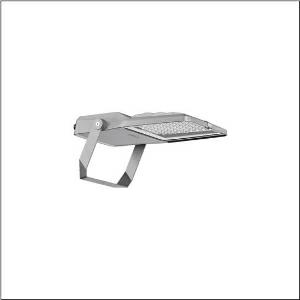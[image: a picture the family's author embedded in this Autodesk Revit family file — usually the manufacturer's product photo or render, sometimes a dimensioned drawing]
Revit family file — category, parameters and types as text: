
# Revit family: floodlight_fl_21_mini___pl52_5xa7773c4d1a_b58d
name_source: partatom
category: Lighting Fixtures
units: mm (PartAtom-declared; Revit-internal decimal feet)

## family parameters
Cut with Voids When Loaded = No
Host = Face
Light Source = No
Part Type = Normal
Room Calculation Point = No
Round Connector Dimension = Use Diameter
Shared = No

## types (1)
- --- (1 x LED, 20360 lm, 163.5 W, 4000K)
    Apparent Load = 163 VA
    CIE Flux Codes = 26 60 98 100 100
    Color Rendering = 70
    Color Temperature = 4000K
    Default Elevation = 1800 mm
    Description = Floodlight FL 21 mini, floodlight, primary light control with lens, of PMMA, primary optical cover: protective disc, of toughened safety glass, transparent, light distribution: PL52, light emission: direct distribution, installation type: surface-mounted, LED, High Power LED, rated luminous flux: 20.360lm, luminous efficacy: 125lm/W, light colour: 740, colour temperature: 4000K, control gear: ON/OFF Multilumen, control: Temp-Guard, with terminal, 6-pole, mains connection: 220..240V, AC, 50/60Hz, start of lifetime: 164W, luminaire housing, of diecast aluminium, powder-coated, Siteco® metallic grey (DB 702S), corrosivity category C5 mid according to DIN EN ISO 12944, suitable for swimming pools, chlorine-resistant, sealing non-destructively replaceable, mounting bracket, of steel, galvanised, powder-coated, Siteco® metallic grey (DB 702S), ON/OFF, protection rating (complete): IP66, insulation class (complete): insulation class I (protective earthing), certification: CE, ENEC, VDE, protection symbol: D, impact resistance: IK08, permissible operating ambient temperature: -40..+40°C, permissible operating ambient temperature for outdoor applications: -40..+50°C, standard: DIN EN 12944, LABS conformity tested according to VDMA 24364:2018-05, packaging unit: 1 piece

Light Distribution: PL52
    Height = 70 mm
    Lamp = 1 x LED
    Lamp Light Flux = 20360 lm
    Lamp Power = 163.5 W
    Lamp count = 1
    Length = 485 mm
    Luminous efficacy = 125 lm/W
    Manufacturer = Siteco
    ModVariant = No
    Model = 5XA7773C4D1A
    Number of Poles = 1
    OnlyDefault = Yes
    Power Factor = 1
    Product Name = Floodlight FL 21 mini | PL52
    Product group = floodlight | pylon annexe
    ProductGroupID = 6200
    Protection Class = Protection class I
    Protection Degree = IP 66
    RLX_Detail_Level = 1
    RLX_Emergency_Light_Flux = 0 lm
    RLX_Emergency_Type = 0
    RLX_Emergency_Type_DB = No
    RlxData = <blob elided: 94457 chars, md5=790c923c>
    Socket = socket
    Standby Power = 0 W
    System Light Flux = 20360 lm
    System Power = 163 W
    Type Comments = factory setting: luminous flux: 100 % | (ON | - | - | - | - | - | - | -) | 825 mA
    Type Image = l_1006845.jpg
    URL = http://relux.com
    VarID = @adj_164092
    Voltage = 0 V
    Weight = 0.00 kg
    Width = 337 mm

## geometry (parser evidence)
native form markers: Blend x4, Sweep x13
no freeform markers — native parametric forms only
